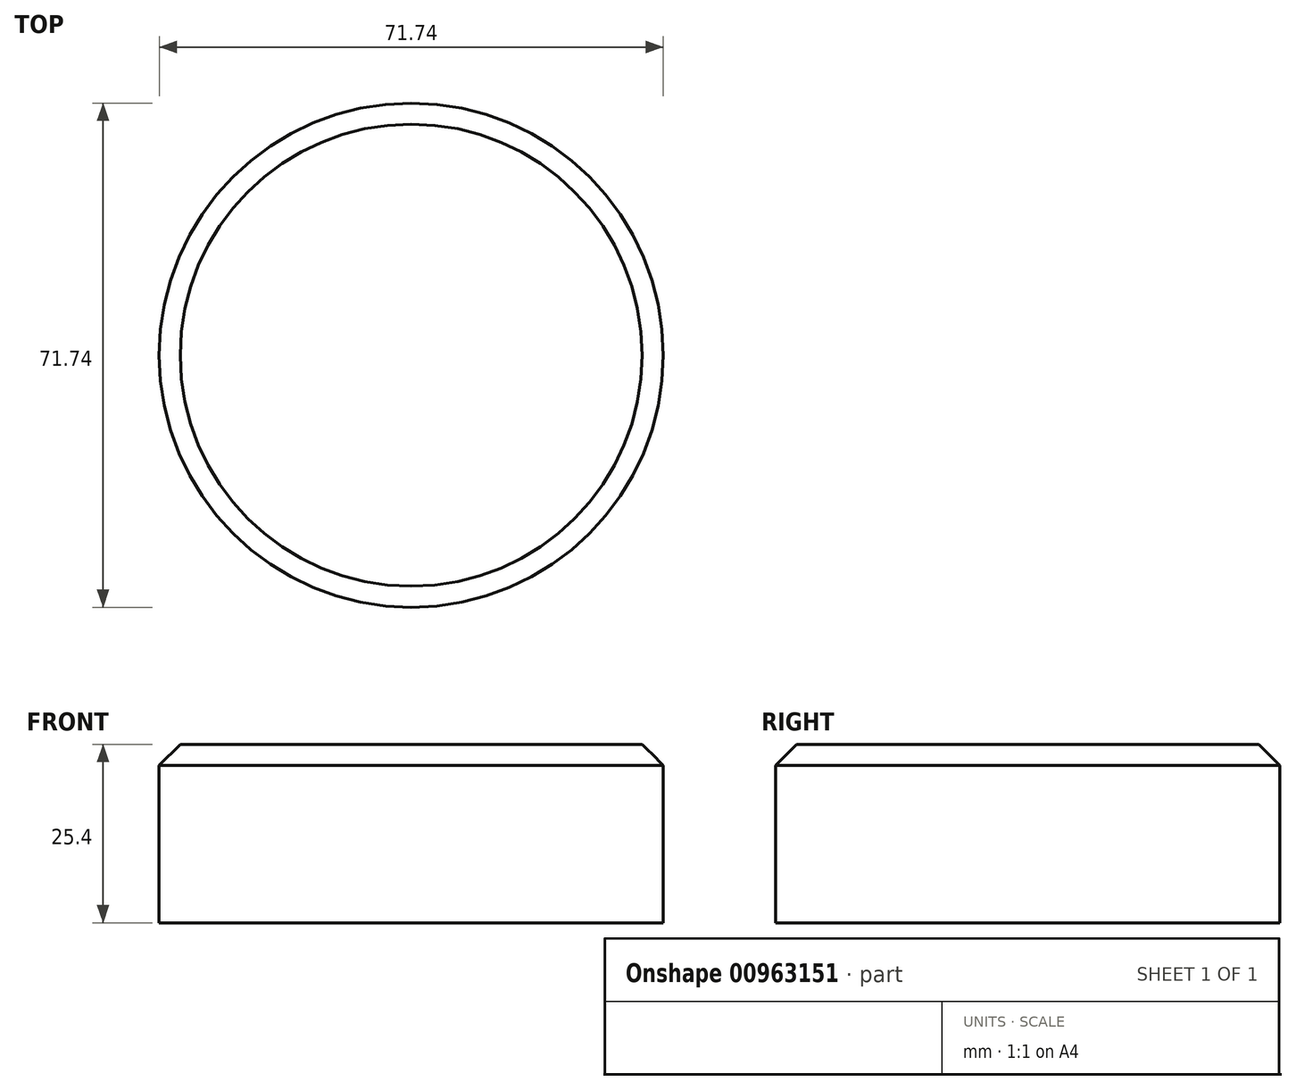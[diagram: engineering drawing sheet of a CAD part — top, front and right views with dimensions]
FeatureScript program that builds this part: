
annotation { "Feature Type Name" : "Feature", "Feature Type Description" : "" }
export const myFeature = defineFeature(function(context is Context, id is Id, definition is map)
    precondition{}
    {
        {
            var Q0;
            Q0=qCreatedBy(makeId("Top.planeOp"),FACE);
            var sketch = newSketch(context, id + "F0", { "sketchPlane" : qUnion([Q0])});
            skCircle(sketch, "E0", {"center": v(0, 0) * mm, "radius": 35.87 * mm});
            skSolve(sketch);
        }
        {
            var Q0;
            Q0 = qSketchRegion(id + "F0", true);
            extrude(context, id + "F1", {"entities" : qUnion([Q0]), "depth" : 25.4 * mm, "offsetDistance" : 25.4 * mm});
        }
        {
            var Q0;
            Q0=makeQuery(id+"F1.opExtrude","CAP_FACE",FACE,{"disambiguationData":[OSD([sQuery(id+"F0.wireOp",EDGE,"E0")])],"isStart":false});
            var sketch = newSketch(context, id + "F2", { "sketchPlane" : qUnion([Q0])});
            skCircle(sketch, "E1.0", {"center": v(0, 0) * mm, "radius": 27.5 * mm});
            skSolve(sketch);
        }
        {
            var Q0;
            Q0=makeQuery(id+"F2.imprint","IMPRINT",FACE,{"disambiguationData":[TD([[makeQuery(id+"F2.imprint","IMPRINT",EDGE,{"derivedFrom":sQuery(id+"F2.wireOp",EDGE,"E1.0")}),1.0]])]});
            cPlane(context, id + "F3", {"entities" : qUnion([Q0]), "cplaneType" : CPlaneType.OFFSET, "offset" : 20 * mm, "width" : 152.4 * mm, "height" : 152.4 * mm});
        }
        {
            var Q0;
            Q0=makeQuery(id+"F1.opExtrude","CAP_EDGE",EDGE,{"disambiguationData":[OSD([sQuery(id+"F0.wireOp",EDGE,"E0")])],"isStart":false});
            chamfer(context, id + "F4", {"entities" : qUnion([Q0]), "width" : 3 * mm, "tangentPropagation" : true});
        }
    });
